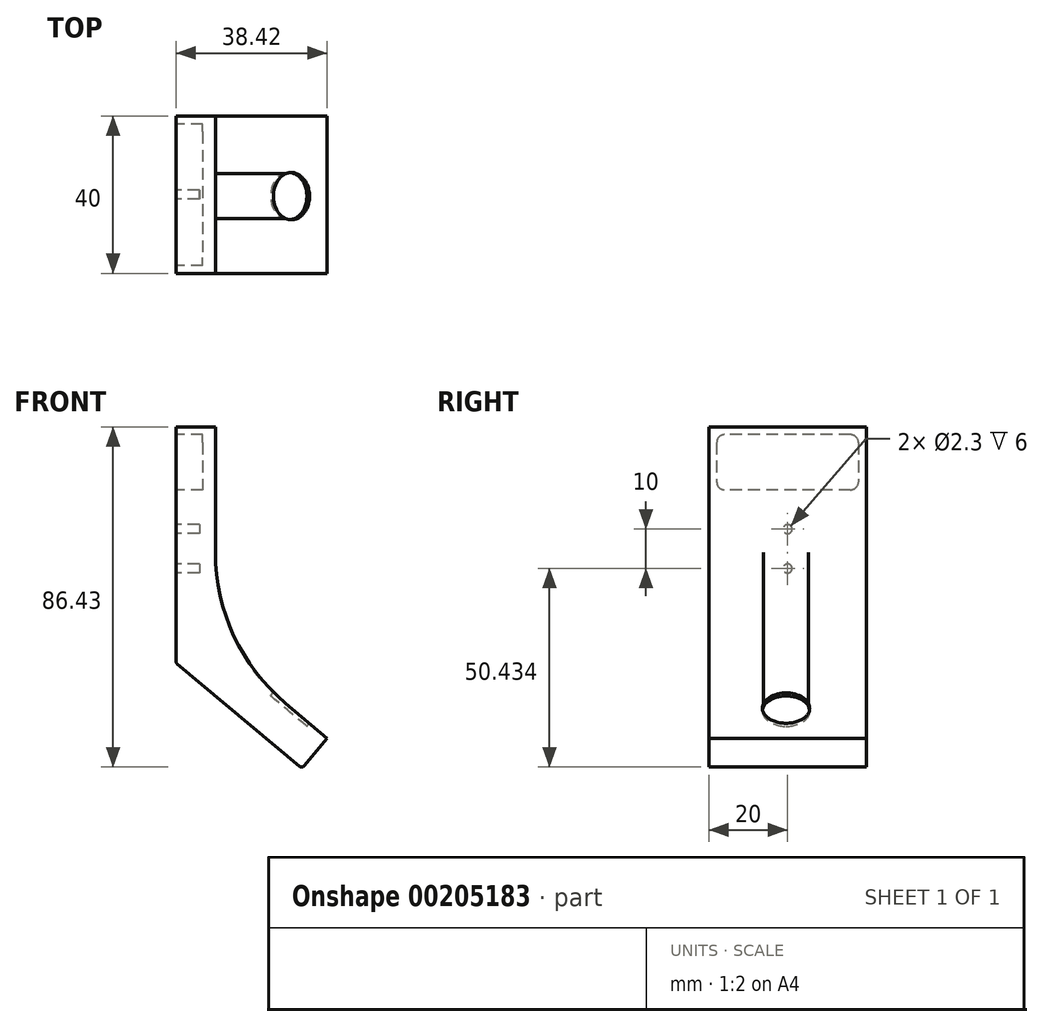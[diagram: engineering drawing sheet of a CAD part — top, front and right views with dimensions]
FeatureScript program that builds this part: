
annotation { "Feature Type Name" : "Feature", "Feature Type Description" : "" }
export const myFeature = defineFeature(function(context is Context, id is Id, definition is map)
    precondition{}
    {
        {
            var Q0;
            Q0=qCreatedBy(makeId("Front.planeOp"),FACE);
            var sketch = newSketch(context, id + "F0", { "sketchPlane" : qUnion([Q0])});
            skLineSegment(sketch, "E0.bottom", {"start": v(0, 59.93) * mm, "end": v(10, 59.93) * mm});
            skLineSegment(sketch, "E0.left", {"start": v(0, 59.93) * mm, "end": v(0, 0) * mm});
            skLineSegment(sketch, "E0.right", {"start": v(10, 59.93) * mm, "end": v(10, 4.66) * mm});
            skPoint(sketch, "E1.visualSharp", {"position": v(0, -20.07) * mm});
            skLineSegment(sketch, "E2", {"start": v(0, 0) * mm, "end": v(32, -26.85) * mm});
            skLineSegment(sketch, "E3", {"start": v(10, 4.66) * mm, "end": v(24.68, -7.65) * mm});
            skLineSegment(sketch, "E4", {"start": v(38.42, -19.19) * mm, "end": v(32, -26.85) * mm});
            skLineSegment(sketch, "E5", {"start": v(24.68, -7.65) * mm, "end": v(38.42, -19.19) * mm});
            skSolve(sketch);
        }
        {
            var Q0;
            Q0 = qSketchRegion(id + "F0", true);
            extrude(context, id + "F1", {"entities" : qUnion([Q0]), "depth" : 40 * mm});
        }
        {
            var Q0;
            Q0=makeQuery(id+"F1.opExtrude","SWEPT_FACE",FACE,{"disambiguationData":[OSD([sQuery(id+"F0.wireOp",EDGE,"E0.right")])]});
            var sketch = newSketch(context, id + "F2", { "sketchPlane" : qUnion([Q0])});
            skText(sketch, "E6", { "text": "Prima", "fontName": "AllertaStencil-Regular.ttf"});
            skLineSegment(sketch, "E7", {"start": v(-20, 59.93) * mm, "end": v(-20, 54.93) * mm, "construction": true});
            const initialGuessF2  = {"E6": [-0.038, 0.0657, 1, 0, 0.0093]};
            skSetInitialGuess(sketch, initialGuessF2);
            skSolve(sketch);
        }
        {
            var Q0;
            Q0 = qSketchRegion(id + "F2", true);
            extrude(context, id + "F3", {"entities" : qUnion([Q0]), "operationType" : NewBodyOperationType.REMOVE, "oppositeDirection" : true, "depth" : 25 * mm});
        }
        {
            var Q0;
            Q0=makeQuery(id+"F1.opExtrude","SWEPT_FACE",FACE,{"disambiguationData":[OSD([sQuery(id+"F0.wireOp",EDGE,"E3"),sQuery(id+"F0.wireOp",EDGE,"E5")])]});
            var sketch = newSketch(context, id + "F4", { "sketchPlane" : qUnion([Q0])});
            skCircle(sketch, "E8", {"center": v(29.87, -20.4) * mm, "radius": 6 * mm});
            skSolve(sketch);
        }
        {
            var Q0;
            Q0 = qSketchRegion(id + "F4", true);
            extrude(context, id + "F5", {"entities" : qUnion([Q0]), "operationType" : NewBodyOperationType.REMOVE, "oppositeDirection" : true, "depth" : 1 * mm});
        }
        {
            var Q0;
            Q0=makeQuery(id+"F1.opExtrude","SWEPT_FACE",FACE,{"disambiguationData":[OSD([sQuery(id+"F0.wireOp",EDGE,"E0.left")])]});
            var sketch = newSketch(context, id + "F6", { "sketchPlane" : qUnion([Q0])});
            skLineSegment(sketch, "E9.bottom", {"start": v(4.02, 57.93) * mm, "end": v(36.02, 57.93) * mm});
            skLineSegment(sketch, "E9.top", {"start": v(4.02, 43.93) * mm, "end": v(36.02, 43.93) * mm});
            skLineSegment(sketch, "E9.left", {"start": v(2.02, 55.93) * mm, "end": v(2.02, 45.93) * mm});
            skLineSegment(sketch, "E9.right", {"start": v(38.02, 55.93) * mm, "end": v(38.02, 45.93) * mm});
            skPoint(sketch, "E10", {"position": v(20.02, 57.93) * mm});
            skPoint(sketch, "E11.visualSharp", {"position": v(2.02, 57.93) * mm});
            skArc(sketch, "E11.filletArc", {"start": v(4.02, 57.93) * mm, "mid": v(2.6, 57.35) * mm, "end": v(2.02, 55.93) * mm});
            skPoint(sketch, "E12.visualSharp", {"position": v(38.02, 57.93) * mm});
            skArc(sketch, "E12.filletArc", {"start": v(38.02, 55.93) * mm, "mid": v(37.44, 57.35) * mm, "end": v(36.02, 57.93) * mm});
            skPoint(sketch, "E13.visualSharp", {"position": v(38.02, 43.93) * mm});
            skArc(sketch, "E13.filletArc", {"start": v(36.02, 43.93) * mm, "mid": v(37.44, 44.52) * mm, "end": v(38.02, 45.93) * mm});
            skPoint(sketch, "E14.visualSharp", {"position": v(2.02, 43.93) * mm});
            skArc(sketch, "E14.filletArc", {"start": v(2.02, 45.93) * mm, "mid": v(2.6, 44.52) * mm, "end": v(4.02, 43.93) * mm});
            skSolve(sketch);
        }
        {
            var Q0;
            Q0 = qSketchRegion(id + "F6", true);
            extrude(context, id + "F7", {"entities" : qUnion([Q0]), "operationType" : NewBodyOperationType.REMOVE, "oppositeDirection" : true, "depth" : 6.8 * mm});
        }
        {
            var Q0;
            Q0=makeQuery(id+"F1.opExtrude","SWEPT_EDGE",EDGE,{"disambiguationData":[OSD([sQuery(id+"F0.wireOp",EDGE,"uzMrqwtn-UoWv-K0EJ-vQdU-1eOVLDVVIeKR.right"),sQuery(id+"F0.wireOp",EDGE,"E2")])]});
            fillet(context, id + "F8", {"entities" : qUnion([Q0]), "radius" : 0.84 * mm, "tangentPropagation" : true, "allowEdgeOverflow" : false});
        }
        {
            var Q0;
            Q0=makeQuery(id+"F6.imprint","IMPRINT",FACE,{"disambiguationData":[TD([[makeQuery(id+"F6.imprint","IMPRINT",EDGE,{"derivedFrom":sQuery(id+"F6.wireOp",EDGE,"E9.bottom")}),1.0]])]});
            var sketch = newSketch(context, id + "F9", { "sketchPlane" : qUnion([Q0])});
            skPoint(sketch, "E15.0", {"position": v(20, 59.93) * mm});
            skLineSegment(sketch, "E16", {"start": v(20, 59.93) * mm, "end": v(20, -0.07) * mm, "construction": true});
            skCircle(sketch, "E17", {"center": v(20, 33.93) * mm, "radius": 1.15 * mm});
            skCircle(sketch, "E18", {"center": v(20, 23.93) * mm, "radius": 1.15 * mm});
            skSolve(sketch);
        }
        {
            var Q0;
            Q0 = qSketchRegion(id + "F9", true);
            extrude(context, id + "F10", {"entities" : qUnion([Q0]), "operationType" : NewBodyOperationType.REMOVE, "oppositeDirection" : true, "depth" : 6 * mm});
        }
        {
            var Q0;
            Q0=makeQuery(id+"F1.opExtrude","SWEPT_EDGE",EDGE,{"disambiguationData":[OSD([sQuery(id+"F0.wireOp",EDGE,"E0.right"),sQuery(id+"F0.wireOp",EDGE,"E3")])]});
            fillet(context, id + "F11", {"entities" : qUnion([Q0]), "radius" : 50 * mm, "tangentPropagation" : true, "allowEdgeOverflow" : false});
        }
    });
